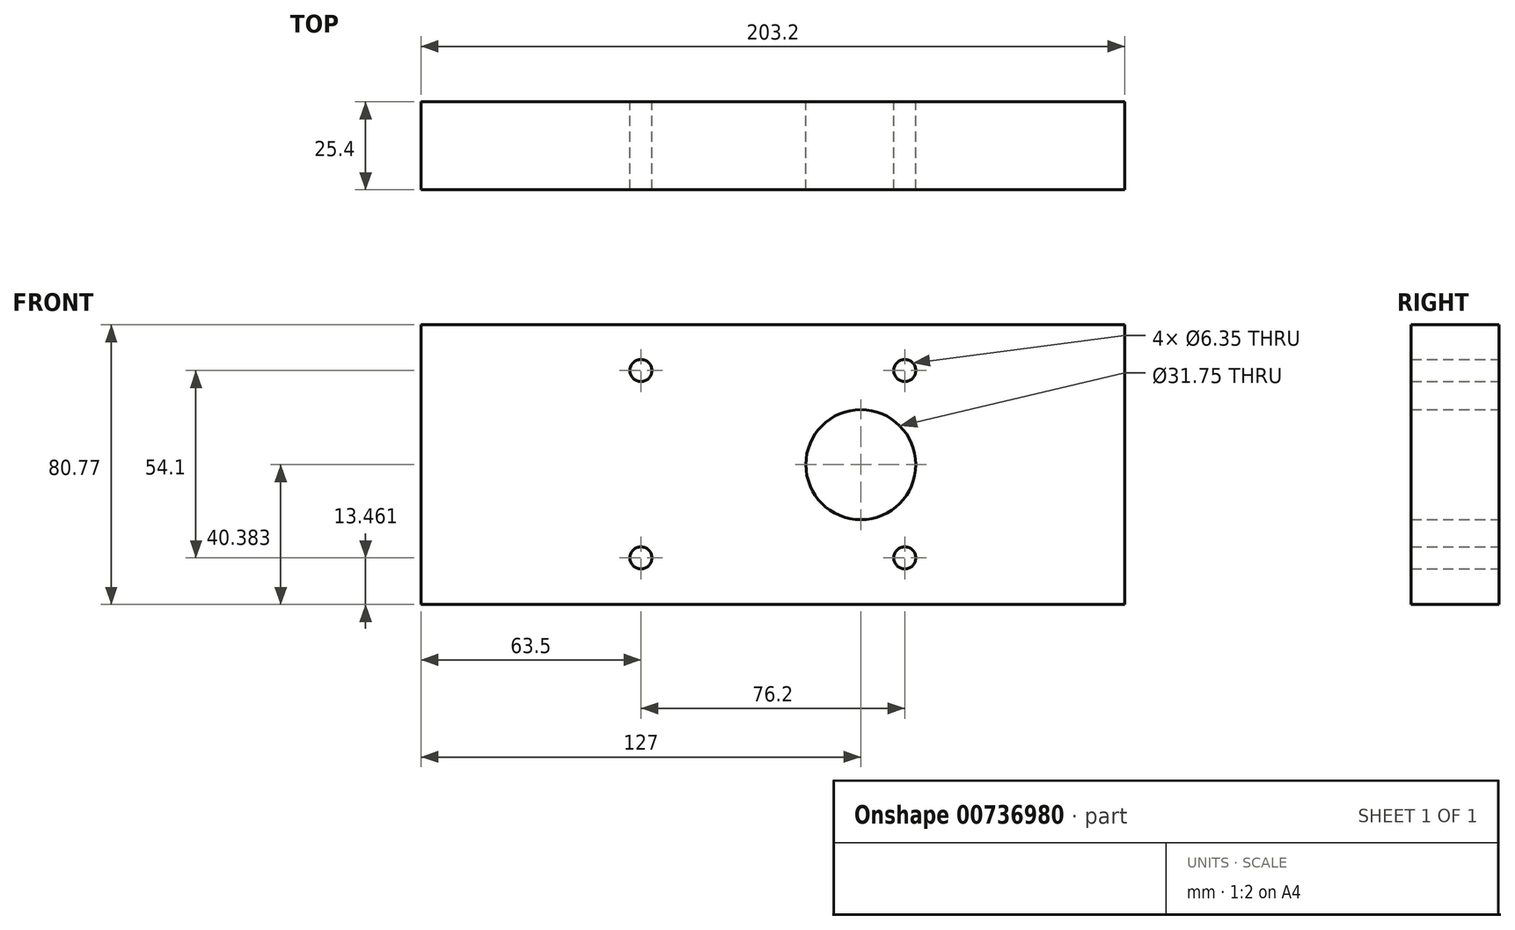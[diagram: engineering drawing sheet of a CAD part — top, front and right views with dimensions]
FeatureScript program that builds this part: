
annotation { "Feature Type Name" : "Feature", "Feature Type Description" : "" }
export const myFeature = defineFeature(function(context is Context, id is Id, definition is map)
    precondition{}
    {
        {
            var Q0;
            Q0=qCreatedBy(makeId("Front.planeOp"),FACE);
            var sketch = newSketch(context, id + "F0", { "sketchPlane" : qUnion([Q0])});
            skLineSegment(sketch, "E0.bottom", {"start": v(-76.2, 24.62) * mm, "end": v(0, 24.62) * mm, "construction": true});
            skLineSegment(sketch, "E0.top", {"start": v(-76.2, -29.48) * mm, "end": v(0, -29.48) * mm, "construction": true});
            skLineSegment(sketch, "E0.left", {"start": v(-76.2, 24.62) * mm, "end": v(-76.2, -29.48) * mm, "construction": true});
            skLineSegment(sketch, "E0.right", {"start": v(0, 24.62) * mm, "end": v(0, -29.48) * mm, "construction": true});
            skPoint(sketch, "E1", {"position": v(-76.2, 24.62) * mm});
            skPoint(sketch, "E2", {"position": v(0, 24.62) * mm});
            skPoint(sketch, "E3", {"position": v(0, -29.48) * mm});
            skPoint(sketch, "E4", {"position": v(-76.2, -29.48) * mm});
            skCircle(sketch, "E5", {"center": v(-76.2, 24.62) * mm, "radius": 3.18 * mm});
            skCircle(sketch, "E6", {"center": v(0, 24.62) * mm, "radius": 3.18 * mm});
            skCircle(sketch, "E7", {"center": v(0, -29.48) * mm, "radius": 3.18 * mm});
            skCircle(sketch, "E8", {"center": v(-76.2, -29.48) * mm, "radius": 3.18 * mm});
            skLineSegment(sketch, "E9.bottom", {"start": v(-139.7, 37.83) * mm, "end": v(63.5, 37.83) * mm});
            skLineSegment(sketch, "E9.top", {"start": v(-139.7, -42.94) * mm, "end": v(63.5, -42.94) * mm});
            skLineSegment(sketch, "E9.left", {"start": v(-139.7, 37.83) * mm, "end": v(-139.7, -42.94) * mm});
            skLineSegment(sketch, "E9.right", {"start": v(63.5, 37.83) * mm, "end": v(63.5, -42.94) * mm});
            skCircle(sketch, "E10", {"center": v(-12.7, -2.56) * mm, "radius": 15.88 * mm});
            skSolve(sketch);
        }
        {
            var Q0;
            Q0 = qSketchRegion(id + "F0", true);
            extrude(context, id + "F1", {"entities" : qUnion([Q0]), "depth" : 25.4 * mm, "offsetDistance" : 25.4 * mm});
        }
    });
